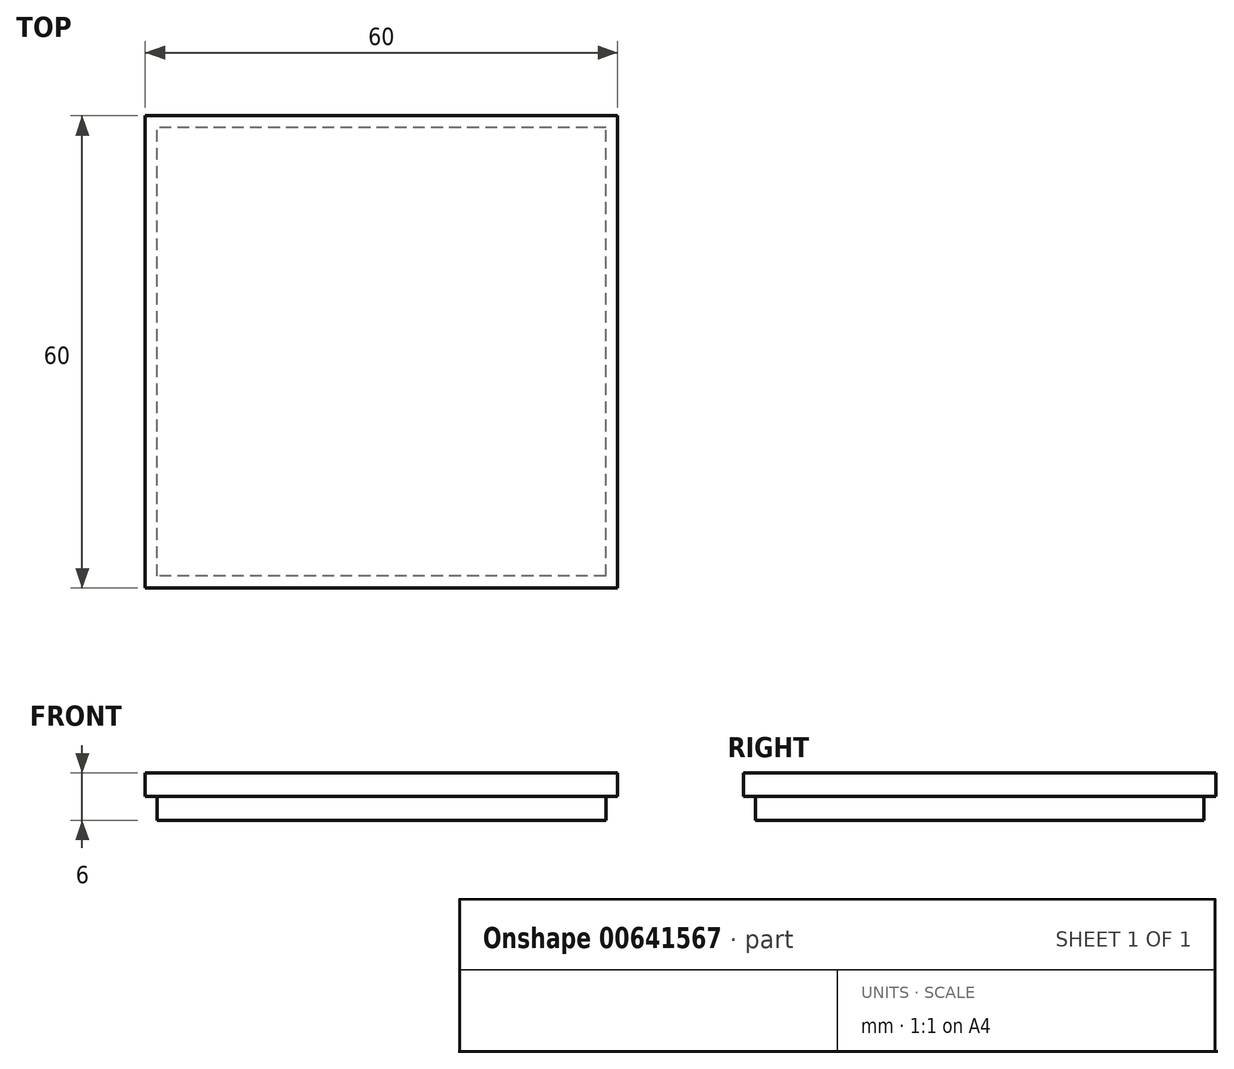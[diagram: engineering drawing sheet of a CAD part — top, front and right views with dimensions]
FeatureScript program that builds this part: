
annotation { "Feature Type Name" : "Feature", "Feature Type Description" : "" }
export const myFeature = defineFeature(function(context is Context, id is Id, definition is map)
    precondition{}
    {
        {
            var Q0;
            Q0=qCreatedBy(makeId("Top.planeOp"),FACE);
            var sketch = newSketch(context, id + "F0", { "sketchPlane" : qUnion([Q0])});
            skLineSegment(sketch, "E0.bottom", {"start": v(30, 30) * mm, "end": v(-30, 30) * mm});
            skLineSegment(sketch, "E0.top", {"start": v(30, -30) * mm, "end": v(-30, -30) * mm});
            skLineSegment(sketch, "E0.left", {"start": v(30, 30) * mm, "end": v(30, -30) * mm});
            skLineSegment(sketch, "E0.right", {"start": v(-30, 30) * mm, "end": v(-30, -30) * mm});
            skPoint(sketch, "E0.middle", {"position": v(0, 0) * mm});
            skSolve(sketch);
        }
        {
            var Q0;
            Q0=makeQuery(id+"F0.imprint","IMPRINT",FACE,{"disambiguationData":[TD([[makeQuery(id+"F0.imprint","IMPRINT",EDGE,{"derivedFrom":sQuery(id+"F0.wireOp",EDGE,"E0.bottom")}),1.0]])]});
            extrude(context, id + "F1", {"entities" : qUnion([Q0]), "depth" : 3 * mm, "offsetDistance" : 25 * mm});
        }
        {
            var Q0;
            Q0=qCreatedBy(makeId("Top.planeOp"),FACE);
            var sketch = newSketch(context, id + "F2", { "sketchPlane" : qUnion([Q0])});
            skLineSegment(sketch, "E1.bottom", {"start": v(28.5, -28.5) * mm, "end": v(-28.5, -28.5) * mm});
            skLineSegment(sketch, "E1.top", {"start": v(28.5, 28.5) * mm, "end": v(-28.5, 28.5) * mm});
            skLineSegment(sketch, "E1.left", {"start": v(28.5, -28.5) * mm, "end": v(28.5, 28.5) * mm});
            skLineSegment(sketch, "E1.right", {"start": v(-28.5, -28.5) * mm, "end": v(-28.5, 28.5) * mm});
            skPoint(sketch, "E1.middle", {"position": v(0, 0) * mm});
            skSolve(sketch);
        }
        {
            var Q0;
            Q0=makeQuery(id+"F2.imprint","IMPRINT",FACE,{"disambiguationData":[TD([[makeQuery(id+"F2.imprint","IMPRINT",EDGE,{"derivedFrom":sQuery(id+"F2.wireOp",EDGE,"E1.bottom")}),-1.0]])]});
            extrude(context, id + "F3", {"entities" : qUnion([Q0]), "operationType" : NewBodyOperationType.ADD, "depth" : -3 * mm, "offsetDistance" : 25 * mm});
        }
    });
